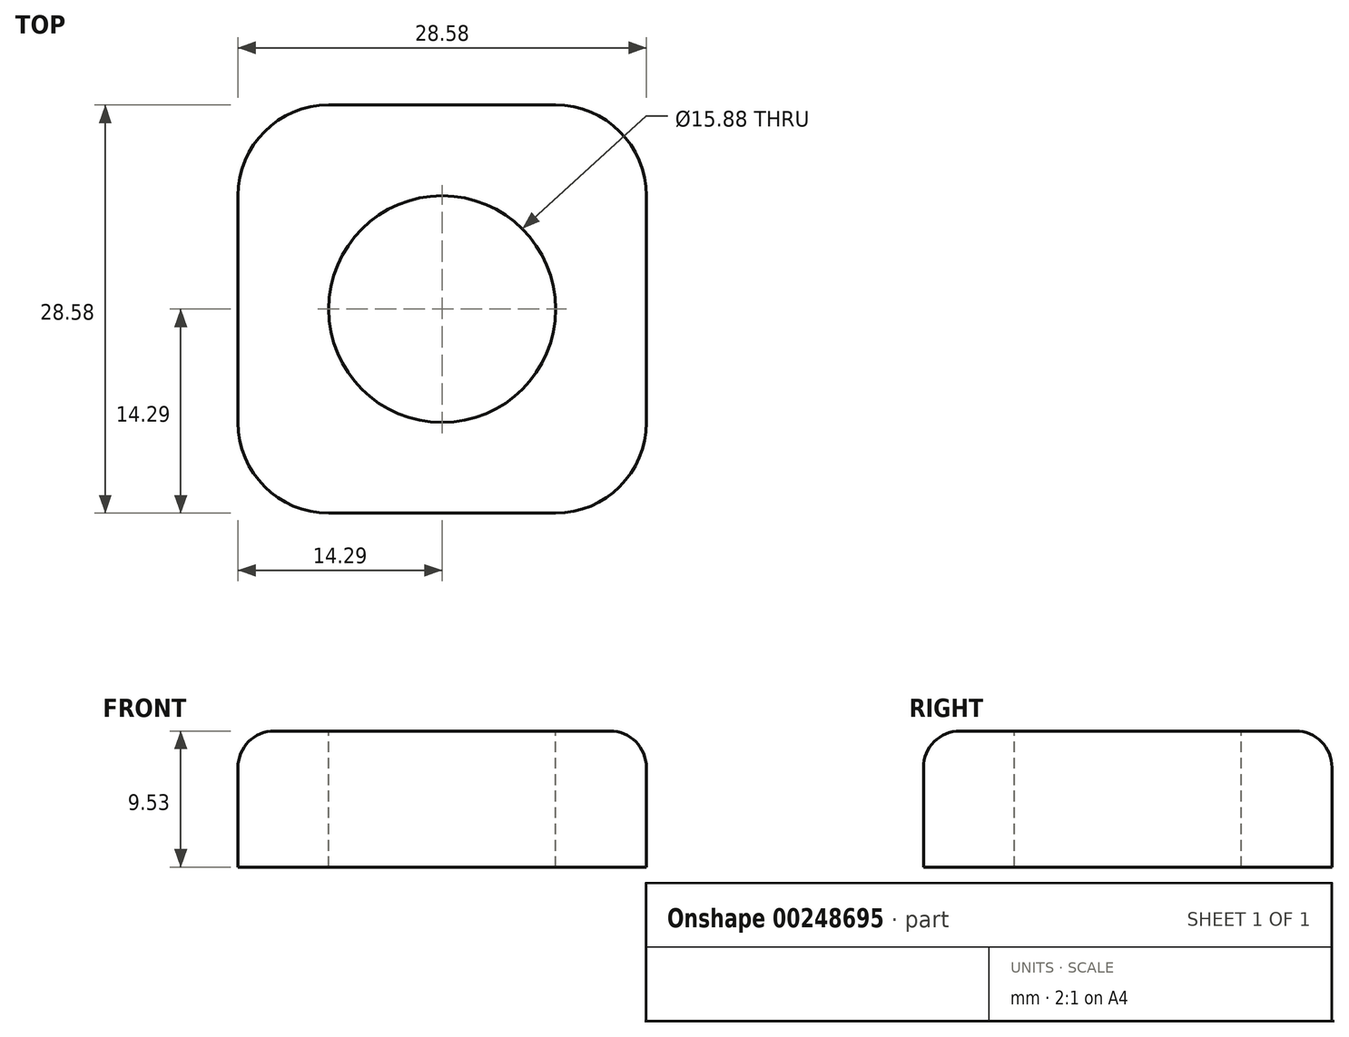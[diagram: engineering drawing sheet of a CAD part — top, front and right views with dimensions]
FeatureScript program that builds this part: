
annotation { "Feature Type Name" : "Feature", "Feature Type Description" : "" }
export const myFeature = defineFeature(function(context is Context, id is Id, definition is map)
    precondition{}
    {
        {
            var Q0;
            Q0=qCreatedBy(makeId("Top.planeOp"),FACE);
            var sketch = newSketch(context, id + "F0", { "sketchPlane" : qUnion([Q0])});
            skLineSegment(sketch, "E0.bottom", {"start": v(14.29, -14.29) * mm, "end": v(-14.29, -14.29) * mm});
            skLineSegment(sketch, "E0.top", {"start": v(14.29, 14.29) * mm, "end": v(-14.29, 14.29) * mm});
            skLineSegment(sketch, "E0.left", {"start": v(14.29, -14.29) * mm, "end": v(14.29, 14.29) * mm});
            skLineSegment(sketch, "E0.right", {"start": v(-14.29, -14.29) * mm, "end": v(-14.29, 14.29) * mm});
            skPoint(sketch, "E0.middle", {"position": v(0, 0) * mm});
            skSolve(sketch);
        }
        {
            var Q0;
            Q0 = qSketchRegion(id + "F0", true);
            extrude(context, id + "F1", {"entities" : qUnion([Q0]), "depth" : 9.52 * mm});
        }
        {
            var Q0;
            Q0=makeQuery(id+"F1.opExtrude","CAP_FACE",FACE,{"disambiguationData":[OSD([sQuery(id+"F0.wireOp",EDGE,"E0.bottom"),sQuery(id+"F0.wireOp",EDGE,"E0.top"),sQuery(id+"F0.wireOp",EDGE,"E0.left"),sQuery(id+"F0.wireOp",EDGE,"E0.right")])],"isStart":false});
            var sketch = newSketch(context, id + "F2", { "sketchPlane" : qUnion([Q0])});
            skCircle(sketch, "E1", {"center": v(0, 0) * mm, "radius": 7.94 * mm});
            skSolve(sketch);
        }
        {
            var Q0;
            Q0 = qSketchRegion(id + "F2", true);
            extrude(context, id + "F3", {"entities" : qUnion([Q0]), "operationType" : NewBodyOperationType.REMOVE, "endBound" : BoundingType.THROUGH_ALL, "oppositeDirection" : true, "depth" : 25.4 * mm});
        }
        {
            var Q0;
            Q0=makeQuery(id+"F1.opExtrude","SWEPT_EDGE",EDGE,{"disambiguationData":[OSD([sQuery(id+"F0.wireOp",EDGE,"E0.bottom"),sQuery(id+"F0.wireOp",EDGE,"E0.right")])]});
            var Q1;
            Q1=makeQuery(id+"F1.opExtrude","SWEPT_EDGE",EDGE,{"disambiguationData":[OSD([sQuery(id+"F0.wireOp",EDGE,"E0.top"),sQuery(id+"F0.wireOp",EDGE,"E0.right")])]});
            var Q2;
            Q2=makeQuery(id+"F1.opExtrude","SWEPT_EDGE",EDGE,{"disambiguationData":[OSD([sQuery(id+"F0.wireOp",EDGE,"E0.bottom"),sQuery(id+"F0.wireOp",EDGE,"E0.left")])]});
            var Q3;
            Q3=makeQuery(id+"F1.opExtrude","SWEPT_EDGE",EDGE,{"disambiguationData":[OSD([sQuery(id+"F0.wireOp",EDGE,"E0.top"),sQuery(id+"F0.wireOp",EDGE,"E0.left")])]});
            fillet(context, id + "F4", {"entities" : qUnion([Q0, Q1, Q2, Q3]), "radius" : 6.35 * mm, "tangentPropagation" : true, "allowEdgeOverflow" : false});
        }
        {
            var Q0;
            Q0=makeQuery(id+"F3.boolean.opBoolean","COPY",EDGE,{"derivedFrom":makeQuery(id+"F3.opExtrude","CAP_EDGE",EDGE,{"disambiguationData":[OSD([sQuery(id+"F2.wireOp",EDGE,"E1")])],"isStart":true})});
            var Q1;
            Q1=makeQuery(id+"F1.opExtrude","CAP_EDGE",EDGE,{"disambiguationData":[OSD([sQuery(id+"F0.wireOp",EDGE,"E0.bottom")])],"isStart":false});
            fillet(context, id + "F5", {"entities" : qUnion([Q0, Q1]), "radius" : 2.54 * mm, "tangentPropagation" : true, "allowEdgeOverflow" : false});
        }
    });
